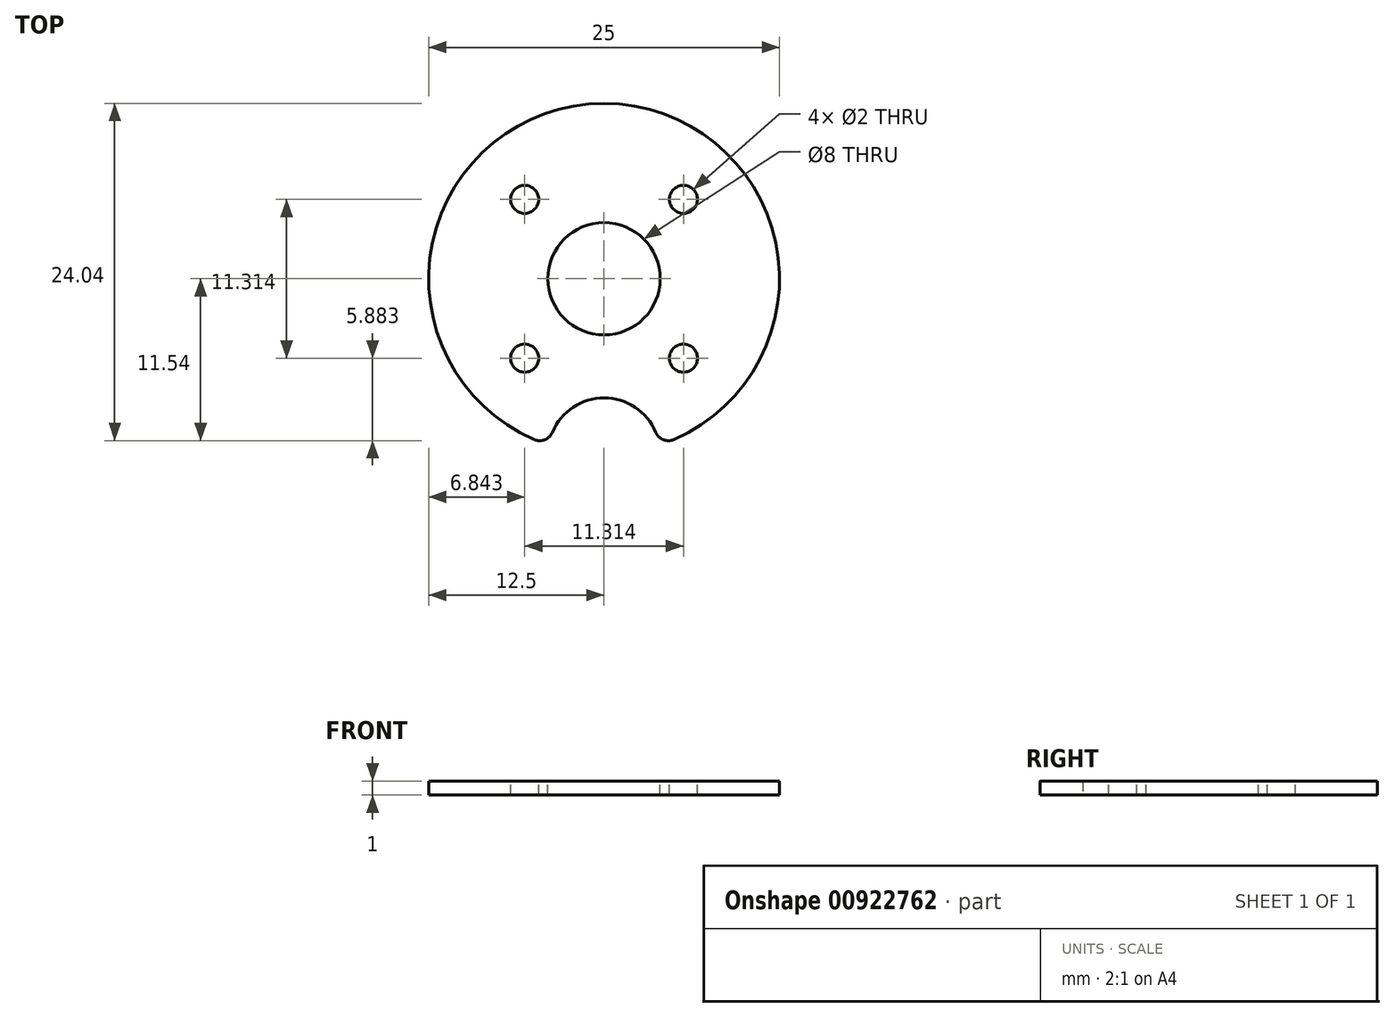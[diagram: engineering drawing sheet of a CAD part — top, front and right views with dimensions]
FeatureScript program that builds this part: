
annotation { "Feature Type Name" : "Feature", "Feature Type Description" : "" }
export const myFeature = defineFeature(function(context is Context, id is Id, definition is map)
    precondition{}
    {
        {
            var Q0;
            Q0=qCreatedBy(makeId("Top.planeOp"),FACE);
            var sketch = newSketch(context, id + "F0", { "sketchPlane" : qUnion([Q0])});
            skCircle(sketch, "E0", {"center": v(0, 0) * mm, "radius": 8 * mm, "construction": true});
            skLineSegment(sketch, "E1.bottom", {"start": v(5.66, -5.66) * mm, "end": v(-5.66, -5.66) * mm, "construction": true});
            skLineSegment(sketch, "E1.top", {"start": v(5.66, 5.66) * mm, "end": v(-5.66, 5.66) * mm, "construction": true});
            skLineSegment(sketch, "E1.left", {"start": v(5.66, -5.66) * mm, "end": v(5.66, 5.66) * mm, "construction": true});
            skLineSegment(sketch, "E1.right", {"start": v(-5.66, -5.66) * mm, "end": v(-5.66, 5.66) * mm, "construction": true});
            skCircle(sketch, "E2", {"center": v(5.66, 5.66) * mm, "radius": 1 * mm, "construction": true});
            skCircle(sketch, "E3.0", {"center": v(5.66, 5.66) * mm, "radius": 1 * mm});
            skCircle(sketch, "E4", {"center": v(0, 0) * mm, "radius": 12.5 * mm});
            skCircle(sketch, "E5.1.0", {"center": v(-5.66, 5.66) * mm, "radius": 1 * mm});
            skCircle(sketch, "E5.2.0", {"center": v(-5.66, -5.66) * mm, "radius": 1 * mm});
            skCircle(sketch, "E5.3.0", {"center": v(5.66, -5.66) * mm, "radius": 1 * mm});
            skCircle(sketch, "E6", {"center": v(0, 0) * mm, "radius": 4 * mm});
            skSolve(sketch);
        }
        {
            var Q0;
            Q0=qCreatedBy(makeId("Front.planeOp"),FACE);
            var sketch = newSketch(context, id + "F1", { "sketchPlane" : qUnion([Q0])});
            skLineSegment(sketch, "E7", {"start": v(0, 0) * mm, "end": v(0, 1) * mm});
            skSolve(sketch);
        }
        {
            var Q0;
            Q0=qCreatedBy(makeId("Top.planeOp"),FACE);
            var sketch = newSketch(context, id + "F2", { "sketchPlane" : qUnion([Q0])});
            skCircle(sketch, "E8.0", {"center": v(0, 0) * mm, "radius": 12.5 * mm, "construction": true});
            skCircle(sketch, "E9", {"center": v(0, -12.5) * mm, "radius": 4 * mm});
            skSolve(sketch);
        }
        {
            var Q0;
            Q0 = qSketchRegion(id + "F0", true);
            var Q1;
            Q1=sQuery(id+"F1.wireOp",EDGE,"E7");
            sweep(context, id + "F3", {"profiles" : qUnion([Q0]), "path" : qUnion([Q1])});
        }
        {
            var Q0;
            Q0 = qSketchRegion(id + "F2", true);
            var Q1;
            Q1=makeQuery(id+"F3.opSweep","CAP_FACE",FACE,{"disambiguationData":[OSD([sQuery(id+"F0.wireOp",EDGE,"E3.0"),sQuery(id+"F0.wireOp",EDGE,"E4"),sQuery(id+"F0.wireOp",EDGE,"E5.1.0"),sQuery(id+"F0.wireOp",EDGE,"E5.2.0"),sQuery(id+"F0.wireOp",EDGE,"E5.3.0"),sQuery(id+"F1.wireOp",VERTEX,"E7.end")])],"isStart":false});
            extrude(context, id + "F4", {"entities" : qUnion([Q0]), "operationType" : NewBodyOperationType.REMOVE, "endBound" : BoundingType.UP_TO_SURFACE, "depth" : 25 * mm, "endBoundEntityFace" : qUnion([Q1]), "offsetDistance" : 25 * mm});
        }
        {
            var Q0;
            Q0=makeQuery(id+"F4.boolean.opBoolean","INTERSECT",EDGE,{"disambiguationData":[OD(0.0)],"derivedFrom":[makeQuery(id+"F3.opSweep","SWEPT_FACE",FACE,{"disambiguationData":[OSD([sQuery(id+"F0.wireOp",EDGE,"E4"),sQuery(id+"F1.wireOp",EDGE,"E7")])]}),makeQuery(id+"F4.opExtrude","SWEPT_FACE",FACE,{"disambiguationData":[OSD([sQuery(id+"F2.wireOp",EDGE,"E9")])]})]});
            var Q1;
            Q1=makeQuery(id+"F4.boolean.opBoolean","INTERSECT",EDGE,{"disambiguationData":[OD(1.0)],"derivedFrom":[makeQuery(id+"F3.opSweep","SWEPT_FACE",FACE,{"disambiguationData":[OSD([sQuery(id+"F0.wireOp",EDGE,"E4"),sQuery(id+"F1.wireOp",EDGE,"E7")])]}),makeQuery(id+"F4.opExtrude","SWEPT_FACE",FACE,{"disambiguationData":[OSD([sQuery(id+"F2.wireOp",EDGE,"E9")])]})]});
            fillet(context, id + "F5", {"entities" : qUnion([Q0, Q1]), "radius" : 1 * mm, "allowEdgeOverflow" : false});
        }
    });
